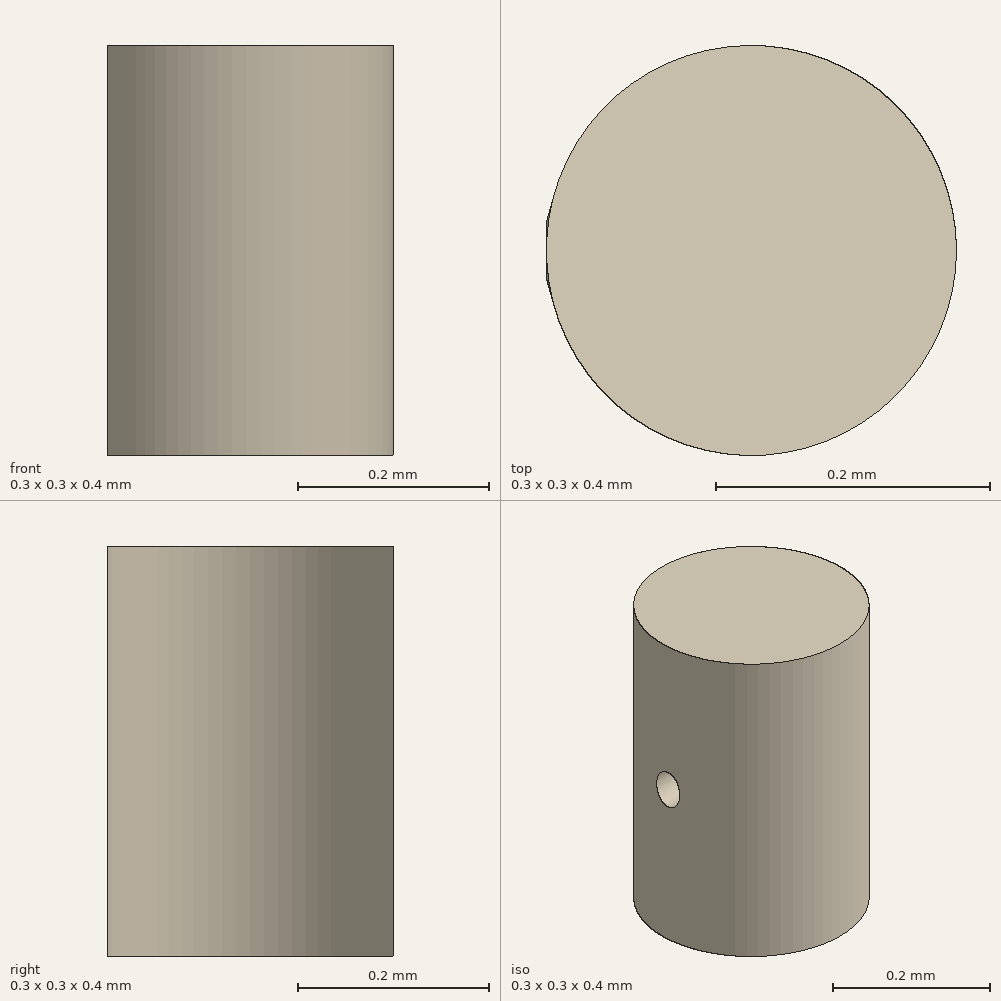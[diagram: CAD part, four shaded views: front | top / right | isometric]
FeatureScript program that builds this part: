
annotation { "Feature Type Name" : "Feature", "Feature Type Description" : "" }
export const myFeature = defineFeature(function(context is Context, id is Id, definition is map)
    precondition{}
    {
        {
            var Q0;
            Q0=qCreatedBy(makeId("Top.planeOp"),FACE);
            var sketch = newSketch(context, id + "F0", { "sketchPlane" : qUnion([Q0])});
            skCircle(sketch, "E0", {"center": v(0, 0) * mm, "radius": 0.15 * mm});
            skSolve(sketch);
        }
        {
            var Q0;
            Q0=qSketchRegion(id+"F0",true);
            extrude(context, id + "F1", {"entities" : qUnion([Q0]), "depth" : 0.43 * mm, "offsetDistance" : 25 * mm});
        }
        {
            var Q0;
            Q0=qCreatedBy(makeId("Top.planeOp"),FACE);
            var sketch = newSketch(context, id + "F2", { "sketchPlane" : qUnion([Q0])});
            skCircle(sketch, "E1", {"center": v(0, 0) * mm, "radius": 0.07 * mm});
            skSolve(sketch);
        }
        {
            var Q0;
            Q0=qSketchRegion(id+"F2",true);
            extrude(context, id + "F3", {"entities" : qUnion([Q0]), "operationType" : NewBodyOperationType.REMOVE, "depth" : 0.03 * mm, "offsetDistance" : 25 * mm});
        }
        {
            var Q0;
            Q0=qCreatedBy(makeId("Front.planeOp"),FACE);
            var sketch = newSketch(context, id + "F4", { "sketchPlane" : qUnion([Q0])});
            skLineSegment(sketch, "E2", {"start": v(0, 0.1) * mm, "end": v(0, 0.25) * mm});
            skLineSegment(sketch, "E3", {"start": v(0, 0.25) * mm, "end": v(0.42, -0.1) * mm, "construction": true});
            skLineSegment(sketch, "E4", {"start": v(0.42, -0.1) * mm, "end": v(0.08, 0.33) * mm, "construction": true});
            skLineSegment(sketch, "E5", {"start": v(0.42, -0.1) * mm, "end": v(-0.08, 0.12) * mm, "construction": true});
            skArc(sketch, "E6", {"start": v(-0.08, 0.12) * mm, "mid": v(-0.02, 0.23) * mm, "end": v(0.08, 0.33) * mm});
            skLineSegment(sketch, "E7", {"start": v(-0.08, 0.12) * mm, "end": v(-0.1, 0.13) * mm});
            skLineSegment(sketch, "E8", {"start": v(-0.1, 0.13) * mm, "end": v(0.06, 0.34) * mm});
            skLineSegment(sketch, "E9", {"start": v(0.06, 0.34) * mm, "end": v(0.08, 0.33) * mm});
            skSolve(sketch);
        }
        {
            var Q0;
            Q0=qSketchRegion(id+"F4",true);
            extrude(context, id + "F5", {"entities" : qUnion([Q0]), "operationType" : NewBodyOperationType.REMOVE, "oppositeDirection" : true, "depth" : 0.03 * mm, "offsetDistance" : 25 * mm});
        }
        {
            var Q0;
            Q0=qSketchRegion(id+"F4",true);
            extrude(context, id + "F6", {"entities" : qUnion([Q0]), "operationType" : NewBodyOperationType.REMOVE, "depth" : 0.03 * mm, "offsetDistance" : 25 * mm});
        }
        {
            var Q0;
            Q0=qCreatedBy(makeId("Right.planeOp"),FACE);
            cPlane(context, id + "F7", {"entities" : qUnion([Q0]), "cplaneType" : CPlaneType.OFFSET, "offset" : 0.15 * mm, "oppositeDirection" : true, "width" : 150 * mm, "height" : 150 * mm});
        }
        {
            var Q0;
            Q0=qCreatedBy(id+"F7.planeOp",FACE);
            var sketch = newSketch(context, id + "F8", { "sketchPlane" : qUnion([Q0])});
            skCircle(sketch, "E10", {"center": v(0, 0.22) * mm, "radius": 0.03 * mm});
            skSolve(sketch);
        }
        {
            var Q0;
            Q0=qSketchRegion(id+"F8",true);
            extrude(context, id + "F9", {"entities" : qUnion([Q0]), "operationType" : NewBodyOperationType.REMOVE, "depth" : 0.08 * mm, "offsetDistance" : 25 * mm});
        }
    });
